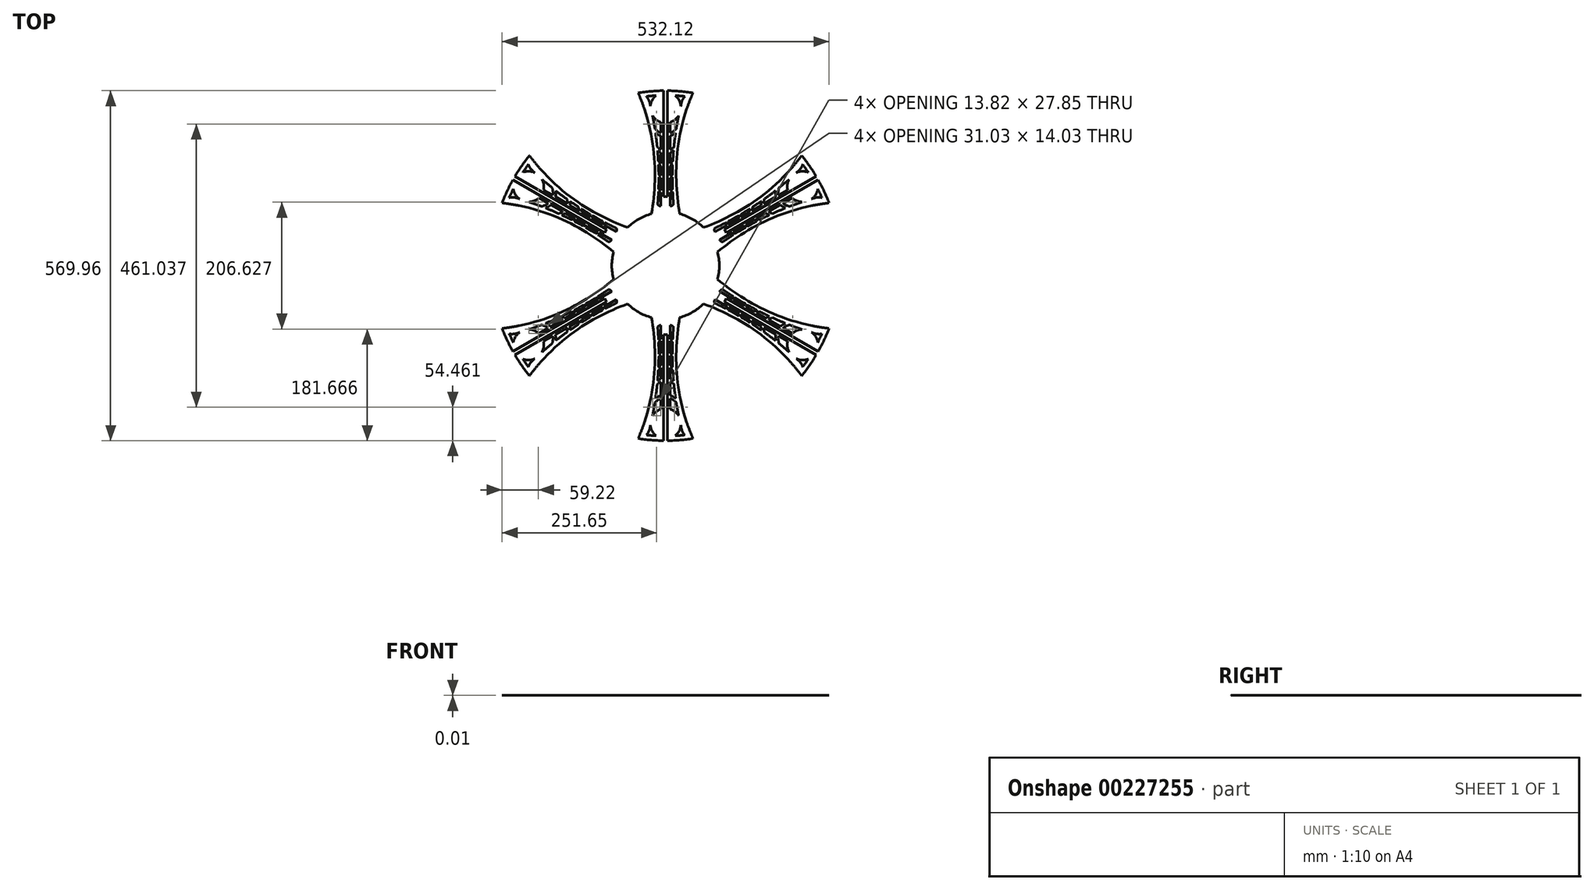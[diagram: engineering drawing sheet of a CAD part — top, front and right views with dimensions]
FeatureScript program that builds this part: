
annotation { "Feature Type Name" : "Feature", "Feature Type Description" : "" }
export const myFeature = defineFeature(function(context is Context, id is Id, definition is map)
    precondition{}
    {
        {
            var Q0;
            Q0=qCreatedBy(makeId("Top.planeOp"),FACE);
            var sketch = newSketch(context, id + "F0", { "sketchPlane" : qUnion([Q0])});
            skCircle(sketch, "E0", {"center": v(0, 0) * mm, "radius": 257.5 * mm});
            skCircle(sketch, "E1", {"center": v(0, 257.5) * mm, "radius": 14 * mm});
            skCircle(sketch, "E2", {"center": v(0, 257.5) * mm, "radius": 25 * mm});
            skCircle(sketch, "E3", {"center": v(0, 0) * mm, "radius": 87.5 * mm});
            skCircle(sketch, "E4", {"center": v(0, 0) * mm, "radius": 285 * mm});
            skFitSpline(sketch, "E5", {"points": [v(-44.56, 281.5) * mm, v(-22.86, 84.46) * mm], "startDerivative": vector(96.87, -225.72) * mm, "endDerivative": vector(-26.7, -166) * mm});
            skFitSpline(sketch, "E6.MirrorCS", {"points": [v(44.56, 281.5) * mm, v(22.86, 84.46) * mm], "startDerivative": vector(-96.87, -225.72) * mm, "endDerivative": vector(26.7, -166) * mm});
            skCircle(sketch, "E7", {"center": v(0, 0) * mm, "radius": 277.5 * mm});
            skFitSpline(sketch, "E8", {"points": [v(-31.39, 275.72) * mm, v(-24.88, 259.9) * mm], "startDerivative": vector(10.09, -7.9) * mm, "endDerivative": vector(0.94, -17.1) * mm});
            skLineSegment(sketch, "E9", {"start": v(-7.5, 233.65) * mm, "end": v(-7.5, 87.18) * mm});
            skFitSpline(sketch, "E10", {"points": [v(-24.92, 259.54) * mm, v(-14.26, 86.33) * mm], "startDerivative": vector(40.4, -153.05) * mm, "endDerivative": vector(-19.5, -161.24) * mm});
            skFitSpline(sketch, "E11", {"points": [v(-17.27, 222.5) * mm, v(-7.5, 216.6) * mm], "startDerivative": vector(12.75, -7.77) * mm, "endDerivative": vector(11.36, -0.15) * mm});
            skFitSpline(sketch, "E12", {"points": [v(-16.28, 215.89) * mm, v(-7.5, 211.53) * mm], "startDerivative": vector(11.3, -6.18) * mm, "endDerivative": vector(13.11, -2.77) * mm});
            skFitSpline(sketch, "E13", {"points": [v(-13.55, 192.8) * mm, v(-7.5, 189.57) * mm], "startDerivative": vector(10.51, -4.51) * mm, "endDerivative": vector(8.22, 1.63) * mm});
            skFitSpline(sketch, "E14", {"points": [v(-13.06, 187.37) * mm, v(-7.5, 184.5) * mm], "startDerivative": vector(8.46, -3.32) * mm, "endDerivative": vector(8.22, 0.77) * mm});
            skFitSpline(sketch, "E15", {"points": [v(-11.9, 170.27) * mm, v(-7.5, 166.5) * mm], "startDerivative": vector(7.9, -2.76) * mm, "endDerivative": vector(6.99, 0.94) * mm});
            skFitSpline(sketch, "E16", {"points": [v(-11.63, 164.66) * mm, v(-7.5, 162.27) * mm], "startDerivative": vector(8.15, 1.33) * mm, "endDerivative": vector(7.18, -0.57) * mm});
            skFitSpline(sketch, "E17", {"points": [v(-11.18, 148.34) * mm, v(-7.5, 146.86) * mm], "startDerivative": vector(4.42, -4.3) * mm, "endDerivative": vector(5.34, 1.4) * mm});
            skFitSpline(sketch, "E18", {"points": [v(-11.14, 143.95) * mm, v(-7.5, 142.75) * mm], "startDerivative": vector(7.94, 0.27) * mm, "endDerivative": vector(5.06, 0.94) * mm});
            skFitSpline(sketch, "E19", {"points": [v(-12.87, 99.75) * mm, v(-7.5, 97.25) * mm], "startDerivative": vector(6.1, -6.48) * mm, "endDerivative": vector(7.74, 0.17) * mm});
            skFitSpline(sketch, "E20", {"points": [v(-11.56, 120.46) * mm, v(-7.5, 119.7) * mm], "startDerivative": vector(5.91, -1.78) * mm, "endDerivative": vector(6.06, 0.37) * mm});
            skFitSpline(sketch, "E21", {"points": [v(-11.4, 124.7) * mm, v(-7.5, 122.76) * mm], "startDerivative": vector(5.42, -3.82) * mm, "endDerivative": vector(5.85, 0.37) * mm});
            skFitSpline(sketch, "E22.MirrorCS", {"points": [v(16.28, 215.89) * mm, v(7.5, 211.53) * mm], "startDerivative": vector(-11.3, -6.18) * mm, "endDerivative": vector(-13.11, -2.77) * mm});
            skFitSpline(sketch, "E23.MirrorCS", {"points": [v(17.27, 222.5) * mm, v(7.5, 216.6) * mm], "startDerivative": vector(-12.75, -7.77) * mm, "endDerivative": vector(-11.36, -0.15) * mm});
            skFitSpline(sketch, "E24.MirrorCS", {"points": [v(13.55, 192.8) * mm, v(7.5, 189.57) * mm], "startDerivative": vector(-10.51, -4.51) * mm, "endDerivative": vector(-8.22, 1.63) * mm});
            skLineSegment(sketch, "E25.MirrorCS", {"start": v(7.5, 233.65) * mm, "end": v(7.5, 87.18) * mm});
            skFitSpline(sketch, "E26.MirrorCS", {"points": [v(13.06, 187.37) * mm, v(7.5, 184.5) * mm], "startDerivative": vector(-8.46, -3.32) * mm, "endDerivative": vector(-8.22, 0.77) * mm});
            skFitSpline(sketch, "E27.MirrorCS", {"points": [v(11.9, 170.27) * mm, v(7.5, 166.5) * mm], "startDerivative": vector(-7.9, -2.76) * mm, "endDerivative": vector(-6.99, 0.94) * mm});
            skFitSpline(sketch, "E28.MirrorCS", {"points": [v(11.63, 164.66) * mm, v(7.5, 162.27) * mm], "startDerivative": vector(-8.15, 1.33) * mm, "endDerivative": vector(-7.18, -0.57) * mm});
            skFitSpline(sketch, "E29.MirrorCS", {"points": [v(11.18, 148.34) * mm, v(7.5, 146.86) * mm], "startDerivative": vector(-4.42, -4.3) * mm, "endDerivative": vector(-5.34, 1.4) * mm});
            skFitSpline(sketch, "E30.MirrorCS", {"points": [v(11.14, 143.95) * mm, v(7.5, 142.75) * mm], "startDerivative": vector(-7.94, 0.27) * mm, "endDerivative": vector(-5.06, 0.94) * mm});
            skFitSpline(sketch, "E31.MirrorCS", {"points": [v(11.4, 124.7) * mm, v(7.5, 122.76) * mm], "startDerivative": vector(-5.42, -3.82) * mm, "endDerivative": vector(-5.85, 0.37) * mm});
            skFitSpline(sketch, "E32.MirrorCS", {"points": [v(11.56, 120.46) * mm, v(7.5, 119.7) * mm], "startDerivative": vector(-5.91, -1.78) * mm, "endDerivative": vector(-6.06, 0.37) * mm});
            skFitSpline(sketch, "E33.MirrorCS", {"points": [v(12.87, 99.75) * mm, v(7.5, 97.25) * mm], "startDerivative": vector(-6.1, -6.48) * mm, "endDerivative": vector(-7.74, 0.17) * mm});
            skFitSpline(sketch, "E34.MirrorCS", {"points": [v(24.92, 259.54) * mm, v(14.26, 86.33) * mm], "startDerivative": vector(-40.4, -153.05) * mm, "endDerivative": vector(19.5, -161.24) * mm});
            skFitSpline(sketch, "E35.MirrorCS", {"points": [v(31.39, 275.72) * mm, v(24.88, 259.9) * mm], "startDerivative": vector(-10.09, -7.9) * mm, "endDerivative": vector(-0.94, -17.1) * mm});
            skLineSegment(sketch, "E36", {"start": v(-3.17, 87.44) * mm, "end": v(-3.18, 284.98) * mm});
            skLineSegment(sketch, "E37.MirrorCS", {"start": v(3.17, 87.44) * mm, "end": v(3.18, 284.98) * mm});
            skLineSegment(sketch, "E38", {"start": v(-3.17, 112.44) * mm, "end": v(3.17, 112.44) * mm});
            skSolve(sketch);
        }
        {
            var Q0;
            {var subQ0=sQuery(id+"F0.wireOp",EDGE,"E2");var subQ1=sQuery(id+"F0.wireOp",EDGE,"E0");var subQ2=makeQuery(id+"F0.imprint","INTERSECT",VERTEX,{"disambiguationData":[OD(0.0)],"derivedFrom":[subQ1,subQ0]});Q0=makeQuery(id+"F0.imprint","IMPRINT",FACE,{"disambiguationData":[TD([[makeQuery(id+"F0.imprint","IMPRINT",EDGE,{"disambiguationData":[TD([[subQ2,-1.0]])],"derivedFrom":subQ1}),-1.0]])]});}
            var Q1;
            {var subQ0=sQuery(id+"F0.wireOp",EDGE,"E1");var subQ1=sQuery(id+"F0.wireOp",EDGE,"E0");var subQ2=makeQuery(id+"F0.imprint","INTERSECT",VERTEX,{"disambiguationData":[OD(0.0)],"derivedFrom":[subQ1,subQ0]});Q1=makeQuery(id+"F0.imprint","IMPRINT",FACE,{"disambiguationData":[TD([[makeQuery(id+"F0.imprint","IMPRINT",EDGE,{"disambiguationData":[TD([[subQ2,-1.0]])],"derivedFrom":subQ1}),-1.0]])]});}
            var Q2;
            {var subQ0=sQuery(id+"F0.wireOp",EDGE,"E1");var subQ1=sQuery(id+"F0.wireOp",EDGE,"E0");var subQ2=makeQuery(id+"F0.imprint","INTERSECT",VERTEX,{"disambiguationData":[OD(0.0)],"derivedFrom":[subQ1,subQ0]});Q2=makeQuery(id+"F0.imprint","IMPRINT",FACE,{"disambiguationData":[TD([[makeQuery(id+"F0.imprint","IMPRINT",EDGE,{"disambiguationData":[TD([[subQ2,-1.0]])],"derivedFrom":subQ1}),1.0]])]});}
            var Q3;
            {var subQ0=sQuery(id+"F0.wireOp",EDGE,"E2");var subQ1=sQuery(id+"F0.wireOp",EDGE,"E0");var subQ2=makeQuery(id+"F0.imprint","INTERSECT",VERTEX,{"disambiguationData":[OD(0.0)],"derivedFrom":[subQ1,subQ0]});Q3=makeQuery(id+"F0.imprint","IMPRINT",FACE,{"disambiguationData":[TD([[makeQuery(id+"F0.imprint","IMPRINT",EDGE,{"disambiguationData":[TD([[subQ2,1.0]])],"derivedFrom":subQ1}),1.0]])]});}
            var Q4;
            {var subQ5=sQuery(id+"F0.wireOp",EDGE,"E0");var subQ7=sQuery(id+"F0.wireOp",EDGE,"E2");var subQ8=makeQuery(id+"F0.imprint","INTERSECT",VERTEX,{"disambiguationData":[OD(0.0)],"derivedFrom":[subQ5,subQ7]});Q4=makeQuery(id+"F0.imprint","IMPRINT",FACE,{"disambiguationData":[TD([[makeQuery(id+"F0.imprint","IMPRINT",EDGE,{"disambiguationData":[TD([[subQ8,1.0]])],"derivedFrom":subQ5}),-1.0]])]});}
            var Q5;
            {var subQ0=sQuery(id+"F0.wireOp",EDGE,"E3");var subQ1=makeQuery(id+"F0.imprint","INTERSECT",VERTEX,{"derivedFrom":[subQ0,sQuery(id+"F0.wireOp",EDGE,"E5")]});Q5=makeQuery(id+"F0.imprint","IMPRINT",FACE,{"disambiguationData":[TD([[makeQuery(id+"F0.imprint","IMPRINT",EDGE,{"disambiguationData":[TD([[subQ1,1.0]])],"derivedFrom":subQ0}),1.0]])]});}
            var Q6;
            {var subQ5=sQuery(id+"F0.wireOp",EDGE,"E8");Q6=makeQuery(id+"F0.imprint","IMPRINT",FACE,{"disambiguationData":[TD([[makeQuery(id+"F0.imprint","IMPRINT",EDGE,{"derivedFrom":subQ5}),-1.0]])]});}
            var Q7;
            {var subQ3=sQuery(id+"F0.wireOp",EDGE,"E2");var subQ4=sQuery(id+"F0.wireOp",EDGE,"E0");var subQ5=makeQuery(id+"F0.imprint","INTERSECT",VERTEX,{"disambiguationData":[OD(1.0)],"derivedFrom":[subQ4,subQ3]});Q7=makeQuery(id+"F0.imprint","IMPRINT",FACE,{"disambiguationData":[TD([[makeQuery(id+"F0.imprint","IMPRINT",EDGE,{"disambiguationData":[TD([[subQ5,-1.0]])],"derivedFrom":subQ4}),1.0]])]});}
            var Q8;
            {var subQ0=sQuery(id+"F0.wireOp",EDGE,"E11");Q8=makeQuery(id+"F0.imprint","IMPRINT",FACE,{"disambiguationData":[TD([[makeQuery(id+"F0.imprint","IMPRINT",EDGE,{"derivedFrom":subQ0}),-1.0]])]});}
            var Q9;
            {var subQ0=sQuery(id+"F0.wireOp",EDGE,"E13");Q9=makeQuery(id+"F0.imprint","IMPRINT",FACE,{"disambiguationData":[TD([[makeQuery(id+"F0.imprint","IMPRINT",EDGE,{"derivedFrom":subQ0}),-1.0]])]});}
            var Q10;
            {var subQ0=sQuery(id+"F0.wireOp",EDGE,"E15");Q10=makeQuery(id+"F0.imprint","IMPRINT",FACE,{"disambiguationData":[TD([[makeQuery(id+"F0.imprint","IMPRINT",EDGE,{"derivedFrom":subQ0}),-1.0]])]});}
            var Q11;
            {var subQ0=sQuery(id+"F0.wireOp",EDGE,"E17");Q11=makeQuery(id+"F0.imprint","IMPRINT",FACE,{"disambiguationData":[TD([[makeQuery(id+"F0.imprint","IMPRINT",EDGE,{"derivedFrom":subQ0}),-1.0]])]});}
            var Q12;
            {var subQ0=sQuery(id+"F0.wireOp",EDGE,"E20");Q12=makeQuery(id+"F0.imprint","IMPRINT",FACE,{"disambiguationData":[TD([[makeQuery(id+"F0.imprint","IMPRINT",EDGE,{"derivedFrom":subQ0}),1.0]])]});}
            var Q13;
            {var subQ5=sQuery(id+"F0.wireOp",EDGE,"E19");Q13=makeQuery(id+"F0.imprint","IMPRINT",FACE,{"disambiguationData":[TD([[makeQuery(id+"F0.imprint","IMPRINT",EDGE,{"derivedFrom":subQ5}),-1.0]])]});}
            var Q14;
            {var subQ0=sQuery(id+"F0.wireOp",EDGE,"E2");var subQ5=sQuery(id+"F0.wireOp",EDGE,"E0");var subQ9=makeQuery(id+"F0.imprint","INTERSECT",VERTEX,{"disambiguationData":[OD(0.0)],"derivedFrom":[subQ5,subQ0]});Q14=makeQuery(id+"F0.imprint","IMPRINT",FACE,{"disambiguationData":[TD([[makeQuery(id+"F0.imprint","IMPRINT",EDGE,{"disambiguationData":[TD([[subQ9,-1.0]])],"derivedFrom":subQ5}),1.0]])]});}
            var Q15;
            {var subQ0=sQuery(id+"F0.wireOp",EDGE,"E10");var subQ1=sQuery(id+"F0.wireOp",EDGE,"E0");var subQ2=makeQuery(id+"F0.imprint","INTERSECT",VERTEX,{"derivedFrom":[subQ1,subQ0]});Q15=makeQuery(id+"F0.imprint","IMPRINT",FACE,{"disambiguationData":[TD([[makeQuery(id+"F0.imprint","IMPRINT",EDGE,{"disambiguationData":[TD([[subQ2,-1.0]])],"derivedFrom":subQ1}),1.0]])]});}
            var Q16;
            {var subQ0=sQuery(id+"F0.wireOp",EDGE,"E10");var subQ1=sQuery(id+"F0.wireOp",EDGE,"E0");var subQ2=makeQuery(id+"F0.imprint","INTERSECT",VERTEX,{"derivedFrom":[subQ1,subQ0]});Q16=makeQuery(id+"F0.imprint","IMPRINT",FACE,{"disambiguationData":[TD([[makeQuery(id+"F0.imprint","IMPRINT",EDGE,{"disambiguationData":[TD([[subQ2,-1.0]])],"derivedFrom":subQ1}),-1.0]])]});}
            var Q17;
            {var subQ1=sQuery(id+"F0.wireOp",EDGE,"E0");var subQ6=sQuery(id+"F0.wireOp",EDGE,"E34.MirrorCS");var subQ7=makeQuery(id+"F0.imprint","INTERSECT",VERTEX,{"derivedFrom":[subQ1,subQ6]});Q17=makeQuery(id+"F0.imprint","IMPRINT",FACE,{"disambiguationData":[TD([[makeQuery(id+"F0.imprint","IMPRINT",EDGE,{"disambiguationData":[TD([[subQ7,-1.0]])],"derivedFrom":subQ1}),1.0]])]});}
            var Q18;
            {var subQ3=sQuery(id+"F0.wireOp",EDGE,"E7");var subQ9=sQuery(id+"F0.wireOp",EDGE,"E2");var subQ10=makeQuery(id+"F0.imprint","INTERSECT",VERTEX,{"disambiguationData":[OD(0.0)],"derivedFrom":[subQ9,subQ3]});Q18=makeQuery(id+"F0.imprint","IMPRINT",FACE,{"disambiguationData":[TD([[makeQuery(id+"F0.imprint","IMPRINT",EDGE,{"disambiguationData":[TD([[subQ10,-1.0]])],"derivedFrom":subQ9}),-1.0]])]});}
            var Q19;
            {var subQ0=sQuery(id+"F0.wireOp",EDGE,"E34.MirrorCS");var subQ6=sQuery(id+"F0.wireOp",EDGE,"E0");var subQ11=makeQuery(id+"F0.imprint","INTERSECT",VERTEX,{"derivedFrom":[subQ6,subQ0]});Q19=makeQuery(id+"F0.imprint","IMPRINT",FACE,{"disambiguationData":[TD([[makeQuery(id+"F0.imprint","IMPRINT",EDGE,{"disambiguationData":[TD([[subQ11,-1.0]])],"derivedFrom":subQ6}),-1.0]])]});}
            var Q20;
            {var subQ0=sQuery(id+"F0.wireOp",EDGE,"E7");var subQ1=sQuery(id+"F0.wireOp",EDGE,"E2");var subQ2=makeQuery(id+"F0.imprint","INTERSECT",VERTEX,{"disambiguationData":[OD(0.0)],"derivedFrom":[subQ1,subQ0]});Q20=makeQuery(id+"F0.imprint","IMPRINT",FACE,{"disambiguationData":[TD([[makeQuery(id+"F0.imprint","IMPRINT",EDGE,{"disambiguationData":[TD([[subQ2,-1.0]])],"derivedFrom":subQ1}),1.0]])]});}
            var Q21;
            {var subQ5=sQuery(id+"F0.wireOp",EDGE,"E9");var subQ19=sQuery(id+"F0.wireOp",EDGE,"E2");var subQ20=makeQuery(id+"F0.imprint","INTERSECT",VERTEX,{"derivedFrom":[subQ19,subQ5]});Q21=makeQuery(id+"F0.imprint","IMPRINT",FACE,{"disambiguationData":[TD([[makeQuery(id+"F0.imprint","IMPRINT",EDGE,{"disambiguationData":[TD([[subQ20,-1.0]])],"derivedFrom":subQ19}),-1.0]])]});}
            var Q22;
            {var subQ0=sQuery(id+"F0.wireOp",EDGE,"E22.MirrorCS");Q22=makeQuery(id+"F0.imprint","IMPRINT",FACE,{"disambiguationData":[TD([[makeQuery(id+"F0.imprint","IMPRINT",EDGE,{"derivedFrom":subQ0}),-1.0]])]});}
            var Q23;
            {var subQ0=sQuery(id+"F0.wireOp",EDGE,"E24.MirrorCS");Q23=makeQuery(id+"F0.imprint","IMPRINT",FACE,{"disambiguationData":[TD([[makeQuery(id+"F0.imprint","IMPRINT",EDGE,{"derivedFrom":subQ0}),1.0]])]});}
            var Q24;
            {var subQ0=sQuery(id+"F0.wireOp",EDGE,"E27.MirrorCS");Q24=makeQuery(id+"F0.imprint","IMPRINT",FACE,{"disambiguationData":[TD([[makeQuery(id+"F0.imprint","IMPRINT",EDGE,{"derivedFrom":subQ0}),1.0]])]});}
            var Q25;
            {var subQ0=sQuery(id+"F0.wireOp",EDGE,"E29.MirrorCS");Q25=makeQuery(id+"F0.imprint","IMPRINT",FACE,{"disambiguationData":[TD([[makeQuery(id+"F0.imprint","IMPRINT",EDGE,{"derivedFrom":subQ0}),1.0]])]});}
            var Q26;
            {var subQ0=sQuery(id+"F0.wireOp",EDGE,"E31.MirrorCS");Q26=makeQuery(id+"F0.imprint","IMPRINT",FACE,{"disambiguationData":[TD([[makeQuery(id+"F0.imprint","IMPRINT",EDGE,{"derivedFrom":subQ0}),1.0]])]});}
            var Q27;
            {var subQ5=sQuery(id+"F0.wireOp",EDGE,"E33.MirrorCS");Q27=makeQuery(id+"F0.imprint","IMPRINT",FACE,{"disambiguationData":[TD([[makeQuery(id+"F0.imprint","IMPRINT",EDGE,{"derivedFrom":subQ5}),1.0]])]});}
            var Q28;
            {var subQ0=sQuery(id+"F0.wireOp",EDGE,"E25.MirrorCS");var subQ11=sQuery(id+"F0.wireOp",EDGE,"E2");var subQ12=makeQuery(id+"F0.imprint","INTERSECT",VERTEX,{"derivedFrom":[subQ11,subQ0]});Q28=makeQuery(id+"F0.imprint","IMPRINT",FACE,{"disambiguationData":[TD([[makeQuery(id+"F0.imprint","IMPRINT",EDGE,{"disambiguationData":[TD([[subQ12,1.0]])],"derivedFrom":subQ11}),-1.0]])]});}
            var Q29;
            {var subQ6=sQuery(id+"F0.wireOp",EDGE,"E1");var subQ7=sQuery(id+"F0.wireOp",EDGE,"E0");var subQ8=makeQuery(id+"F0.imprint","INTERSECT",VERTEX,{"disambiguationData":[OD(1.0)],"derivedFrom":[subQ7,subQ6]});Q29=makeQuery(id+"F0.imprint","IMPRINT",FACE,{"disambiguationData":[TD([[makeQuery(id+"F0.imprint","IMPRINT",EDGE,{"disambiguationData":[TD([[subQ8,-1.0]])],"derivedFrom":subQ7}),1.0]])]});}
            var Q30;
            {var subQ0=sQuery(id+"F0.wireOp",EDGE,"E36");var subQ1=sQuery(id+"F0.wireOp",EDGE,"E0");var subQ2=makeQuery(id+"F0.imprint","INTERSECT",VERTEX,{"derivedFrom":[subQ1,subQ0]});Q30=makeQuery(id+"F0.imprint","IMPRINT",FACE,{"disambiguationData":[TD([[makeQuery(id+"F0.imprint","IMPRINT",EDGE,{"disambiguationData":[TD([[subQ2,-1.0]])],"derivedFrom":subQ1}),1.0]])]});}
            var Q31;
            {var subQ0=sQuery(id+"F0.wireOp",EDGE,"E36");var subQ1=sQuery(id+"F0.wireOp",EDGE,"E0");var subQ2=makeQuery(id+"F0.imprint","INTERSECT",VERTEX,{"derivedFrom":[subQ1,subQ0]});Q31=makeQuery(id+"F0.imprint","IMPRINT",FACE,{"disambiguationData":[TD([[makeQuery(id+"F0.imprint","IMPRINT",EDGE,{"disambiguationData":[TD([[subQ2,-1.0]])],"derivedFrom":subQ1}),-1.0]])]});}
            var Q32;
            {var subQ0=sQuery(id+"F0.wireOp",EDGE,"E1");var subQ1=sQuery(id+"F0.wireOp",EDGE,"E0");var subQ2=makeQuery(id+"F0.imprint","INTERSECT",VERTEX,{"disambiguationData":[OD(1.0)],"derivedFrom":[subQ1,subQ0]});Q32=makeQuery(id+"F0.imprint","IMPRINT",FACE,{"disambiguationData":[TD([[makeQuery(id+"F0.imprint","IMPRINT",EDGE,{"disambiguationData":[TD([[subQ2,-1.0]])],"derivedFrom":subQ1}),-1.0]])]});}
            var Q33;
            {var subQ0=sQuery(id+"F0.wireOp",EDGE,"E36");var subQ1=sQuery(id+"F0.wireOp",EDGE,"E2");var subQ2=makeQuery(id+"F0.imprint","INTERSECT",VERTEX,{"disambiguationData":[OD(0.0)],"derivedFrom":[subQ1,subQ0]});Q33=makeQuery(id+"F0.imprint","IMPRINT",FACE,{"disambiguationData":[TD([[makeQuery(id+"F0.imprint","IMPRINT",EDGE,{"disambiguationData":[TD([[subQ2,-1.0]])],"derivedFrom":subQ1}),1.0]])]});}
            var Q34;
            {var subQ2=sQuery(id+"F0.wireOp",EDGE,"E2");var subQ4=sQuery(id+"F0.wireOp",EDGE,"E36");var subQ7=makeQuery(id+"F0.imprint","INTERSECT",VERTEX,{"disambiguationData":[OD(0.0)],"derivedFrom":[subQ2,subQ4]});Q34=makeQuery(id+"F0.imprint","IMPRINT",FACE,{"disambiguationData":[TD([[makeQuery(id+"F0.imprint","IMPRINT",EDGE,{"disambiguationData":[TD([[subQ7,-1.0]])],"derivedFrom":subQ2}),-1.0]])]});}
            var Q35;
            {var subQ5=sQuery(id+"F0.wireOp",EDGE,"E38");Q35=makeQuery(id+"F0.imprint","IMPRINT",FACE,{"disambiguationData":[TD([[makeQuery(id+"F0.imprint","IMPRINT",EDGE,{"derivedFrom":subQ5}),-1.0]])]});}
            extrude(context, id + "F1", {"entities" : qUnion([Q0, Q1, Q2, Q3, Q4, Q5, Q6, Q7, Q8, Q9, Q10, Q11, Q12, Q13, Q14, Q15, Q16, Q17, Q18, Q19, Q20, Q21, Q22, Q23, Q24, Q25, Q26, Q27, Q28, Q29, Q30, Q31, Q32, Q33, Q34, Q35]), "oppositeDirection" : true, "depth" : 1 / 101.6 * mm});
        }
        {
            var Q0;
            Q0=makeQuery(id+"F1.opExtrude","SWEPT_BODY",BODY,{"disambiguationData":[OSD([sQuery(id+"F0.wireOp",EDGE,"E3"),sQuery(id+"F0.wireOp",EDGE,"E4"),sQuery(id+"F0.wireOp",EDGE,"E5"),sQuery(id+"F0.wireOp",EDGE,"E6.MirrorCS")])]});
            var Q1;
            {var subQ0=sQuery(id+"F0.wireOp",EDGE,"E3");Q1=makeQuery(id+"F1.opExtrude","SWEPT_FACE",FACE,{"disambiguationData":[OSD([subQ0]),TDD([makeQuery(id+"F0.imprint","IMPRINT",EDGE,{"disambiguationData":[TD([[makeQuery(id+"F0.imprint","INTERSECT",VERTEX,{"derivedFrom":[subQ0,sQuery(id+"F0.wireOp",EDGE,"E5")]}),-1.0]])],"derivedFrom":subQ0})])]});}
            circularPattern(context, id + "F2", {"operationType" : NewBodyOperationType.ADD, "entities" : qUnion([Q0]), "axis" : qUnion([Q1]), "angle" : 360 * degree, "instanceCount" : 6, "equalSpace" : true});
        }
    });
